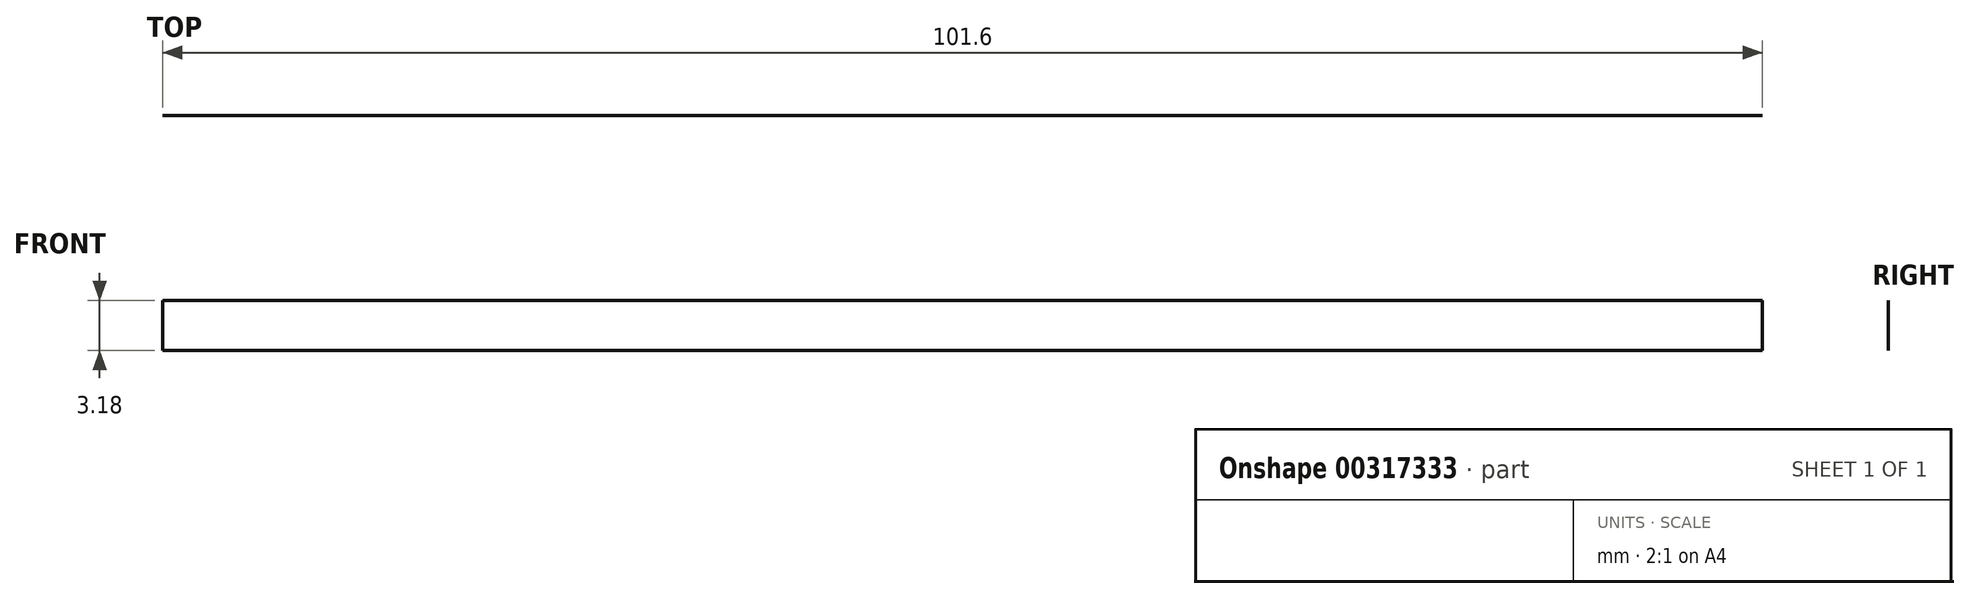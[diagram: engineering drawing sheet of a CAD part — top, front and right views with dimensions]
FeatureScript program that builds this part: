
annotation { "Feature Type Name" : "Feature", "Feature Type Description" : "" }
export const myFeature = defineFeature(function(context is Context, id is Id, definition is map)
    precondition{}
    {
        {
            var Q0;
            Q0=qCreatedBy(makeId("Front.planeOp"),FACE);
            var sketch = newSketch(context, id + "F0", { "sketchPlane" : qUnion([Q0])});
            skLineSegment(sketch, "E0.bottom", {"start": v(-50.8, 1.59) * mm, "end": v(50.8, 1.59) * mm});
            skLineSegment(sketch, "E0.top", {"start": v(-50.8, -1.59) * mm, "end": v(50.8, -1.59) * mm});
            skLineSegment(sketch, "E0.left", {"start": v(-50.8, 1.59) * mm, "end": v(-50.8, -1.59) * mm});
            skLineSegment(sketch, "E0.right", {"start": v(50.8, 1.59) * mm, "end": v(50.8, -1.59) * mm});
            skPoint(sketch, "E0.middle", {"position": v(0, 0) * mm});
            skSolve(sketch);
        }
        {
            var Q0;
            Q0 = qSketchRegion(id + "F0", true);
            extrude(context, id + "F1", {"entities" : qUnion([Q0]), "depth" : 1 / 203.2 * mm});
        }
    });
